# Revit family: Haworth_Lana_Table_Light
name_source: partatom
category: Lighting Fixtures
revit_build: Autodesk Revit 2018 (Build: 20170223_1515(x64)
units: mm (PartAtom-declared; Revit-internal decimal feet)

## family parameters
Always vertical = Yes
Cut with Voids When Loaded = No
Light Source = Yes
OmniClass Number = 23.80.70.11.14
OmniClass Title = General Luminaries, Directional
Part Type = Normal
Room Calculation Point = No
Round Connector Dimension = Use Diameter
Shared = No
Work Plane-Based = No

## types (6) — shared parameters
Assembly Code = D5020200
Base Finish = Haworth _ Metal _ Chrome
Color Filter = 16777215
Dimming Lamp Color Temperature Shift = Incandescent Lamp Curve
Emit Shape Visible in Rendering = No
Emit from Circle Diameter = 24"
Glass Finish = Haworth _ Glass _ Clear
Interior Finish = Haworth _ Grey _ Interior
Light Source Symbol Length = 12"
Manufacturer = Haworth
Revision Number = 1
Size = Verify Final Dim. w/Haworth
Spot Beam Angle = 30.00°
Spot Field Angle = 60.00°
Stand Top Radius = 177/256"
Tilt Angle = 90.00°
URL = http://www.haworth.com
URL - Product = https://www.haworth.com
Warranty = https://www.haworth.com

## per-type parameters (varying)
| type | Actual Depth | Actual Width | Circle Base Radius | Circle Top Radius | Description | Desk Lamp | Large | Medium | Model | Small | Stand Height | Stand Inside Radius | Stand Radius | Stand Top Height | Steel Metal Plate |
| HCPL-LNT3-13 | 13" | 13" | 6 1/2" | 3 3/4" | Haworth Lana Light Large Table Light | Yes | Yes | No | HCPL-LNT3-13 | No | 25" | 5 1/4" | 5 1/2" | 24 79/256" | No |
| HCPL-LNT2-11 | 11" | 11" | 5 109/128" | 4" | Haworth Lana Light Medium Table Light | Yes | No | Yes | HCPL-LNT2-11 | No | 20 1/2" | 4 1/2" | 4 3/4" | 19 207/256" | No |
| HCPL-LNT1-08 | 8 1/2" | 8 1/2" | 5" | 2 3/8" | Haworth Lana Light Small Table Light | Yes | No | No | HCPL-LNT1-08 | Yes | 20 1/2" | 4" | 4 1/4" | 19 207/256" | No |
| HCPL-LNS1-08 | 8 1/2" | 8 1/2" | 5" | 2 3/8" | Haworth Lana Light Small Shade | No | No | No | HCPL-LNS1-08 | Yes | 20 1/2" | 4" | 4 1/4" | 19 207/256" | Yes |
| HCPL-LNS2-11 | 11" | 11" | 5 109/128" | 4" | Haworth Lana Light Medium Shade | No | No | Yes | HCPL-LNS2-11 | No | 20 1/2" | 4 1/2" | 4 3/4" | 19 207/256" | Yes |
| HCPL-LNS3-13 | 13" | 13" | 6 1/2" | 3 3/4" | Haworth Lana Light Large Shade | No | Yes | No | HCPL-LNS3-11 | No | 25" | 5 1/4" | 5 1/2" | 24 79/256" | Yes |

## geometry (parser evidence)
native form markers: Sweep x6
no freeform markers — native parametric forms only
